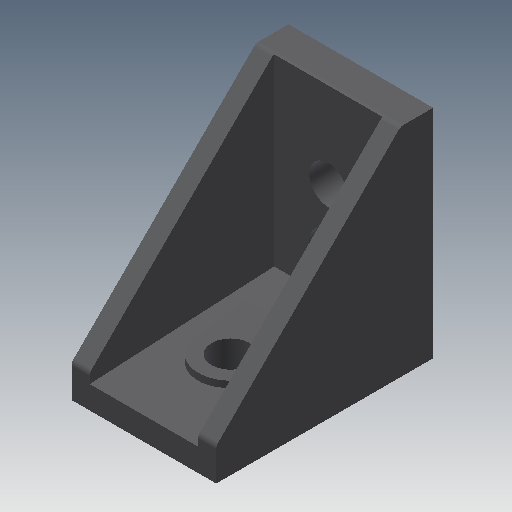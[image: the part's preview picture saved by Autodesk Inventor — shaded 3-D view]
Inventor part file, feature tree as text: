
AUTODESK INVENTOR PART (.ipt)
format: ipt  version: 2018 (Build 220112000, 112)  size: 227,840 bytes
history: native  units: mm
features: other x42, sketch x10, extrude x7, hole x3
ambient origin geometry x8: Origin, YZ Plane, XZ Plane, XY Plane, X Axis, Y Axis, Z Axis, Center Point
bodies: Solid1 (feature_tree)
feature tree (62):
  extrude  "Extrusion1"  Depth=15.0mm TaperAngle=0.0deg
  extrude  "Extrusion2"  Depth=1.0mm TaperAngle=0.0deg
  extrude  "Extrusion3"  Depth=1.0mm TaperAngle=0.0deg
  hole  "Hole1"  [1 undecoded]
  hole  "Hole2"  [1 undecoded]
  hole  "Hole3"  [1 undecoded]
  extrude  "Extrusion4"  [1 undecoded]
  extrude  "Extrusion5"  [1 undecoded]
  extrude  "Extrusion6"  [1 undecoded]
  extrude  "Extrusion7"  [1 undecoded]
  other  "bracket_to_bolt_XY"
  other  "bracket_to_bolt_YZ"
  other  "bracket_to_bolt_ZX"
  other  "bracket_to_bolt_X"
  other  "bracket_to_bolt_Y"
  other  "bracket_to_bolt_Z"
  other  "bracket_to_bolt_Center"
  other  "bracket_to_dummy_XY"
  other  "bracket_to_dummy_YZ"
  other  "bracket_to_dummy_ZX"
  other  "bracket_to_dummy_X"
  other  "bracket_to_dummy_Y"
  other  "bracket_to_dummy_Z"
  other  "bracket_to_dummy_Center"
  other  "to_bolt_4_7_base_XY"
  other  "to_bolt_4_7_base_YZ"
  other  "to_bolt_4_7_base_ZX"
  other  "to_bolt_4_7_base_X"
  other  "to_bolt_4_7_base_Y"
  other  "to_bolt_4_7_base_Z"
  other  "to_bolt_4_7_base_Center"
  other  "to_bolt_row_4_to_7_XY"
  other  "to_bolt_row_4_to_7_YZ"
  other  "to_bolt_row_4_to_7_ZX"
  other  "to_bolt_row_4_to_7_X"
  other  "to_bolt_row_4_to_7_Y"
  other  "to_bolt_row_4_to_7_Z"
  other  "to_bolt_row_4_to_7_Center"
  other  "to_nut_base_4_7_XY"
  other  "to_nut_base_4_7_YZ"
  other  "to_nut_base_4_7_ZX"
  other  "to_nut_base_4_7_X"
  other  "to_nut_base_4_7_Y"
  other  "to_nut_base_4_7_Z"
  other  "to_nut_base_4_7_Center"
  other  "to_nut_row_4_to_7_XY"
  other  "to_nut_row_4_to_7_YZ"
  other  "to_nut_row_4_to_7_ZX"
  other  "to_nut_row_4_to_7_X"
  other  "to_nut_row_4_to_7_Y"
  other  "to_nut_row_4_to_7_Z"
  other  "to_nut_row_4_to_7_Center"
  sketch  "Sketch_15"
  sketch  "Sketch_16"
  sketch  "Sketch_17"
  sketch  "Sketch4"  dims[d4=2.25mm d5=0.0mm]
  sketch  "Sketch5"  dims[d13=5.3mm d14=6.0mm d15=4.0mm d16=2.0mm d17=90.0deg d18=4.5mm d19=0.0mm]
  sketch  "Sketch6"  dims[d20=5.3mm d21=6.0mm d22=4.0mm d23=2.0mm d24=90.0deg d25=4.5mm d26=0.0mm d27=1.0mm d28=0.0mm]
  sketch  "Sketch_1"  dims[d0=20.0mm d1=0.0mm d2=15.0mm d3=0.0mm]
  sketch  "Sketch_4"  dims[d6=5.3mm d7=6.0mm d8=4.0mm d9=2.0mm d10=90.0deg d11=4.5mm d12=0.0mm]
  sketch  "Sketch_10"  dims[d29=1.0mm d30=0.0mm d31=1.0mm d32=0.0mm]
  sketch  "Sketch_11"  dims[d33=1.0mm d34=0.0mm]
note: 7 required parameter values undecoded (feature->parameter linkage not recoverable at this tier; creation-order binding heuristic only, values carry confidence <= 0.55)
